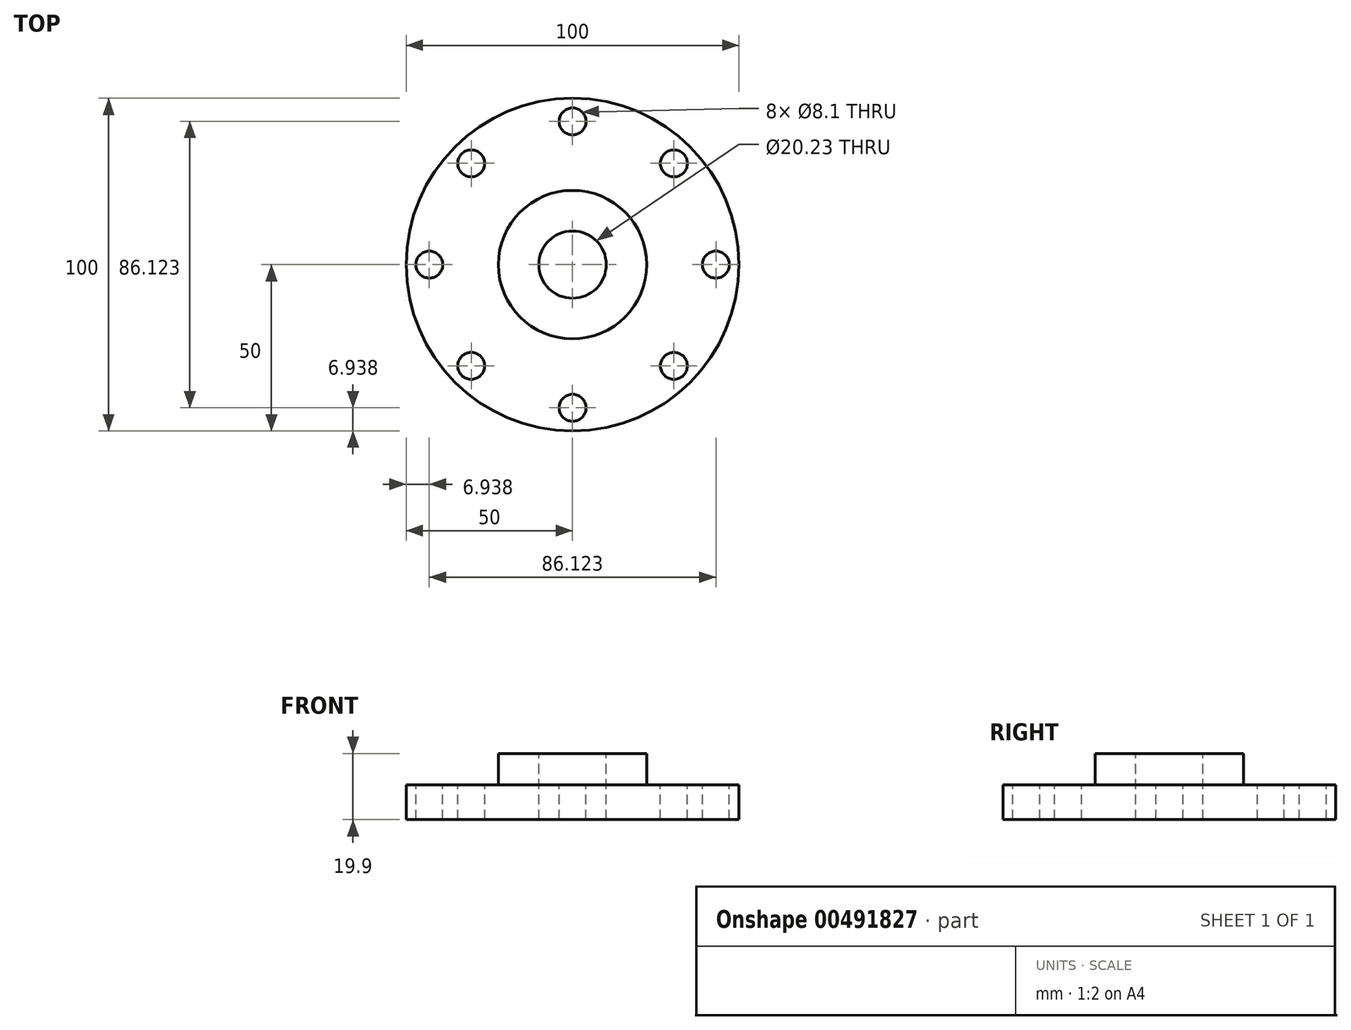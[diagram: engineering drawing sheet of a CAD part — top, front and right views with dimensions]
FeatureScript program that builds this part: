
annotation { "Feature Type Name" : "Feature", "Feature Type Description" : "" }
export const myFeature = defineFeature(function(context is Context, id is Id, definition is map)
    precondition{}
    {
        {
            var Q0;
            Q0=qCreatedBy(makeId("Top.planeOp"),FACE);
            var sketch = newSketch(context, id + "F0", { "sketchPlane" : qUnion([Q0])});
            skCircle(sketch, "E0", {"center": v(0, 0) * mm, "radius": 50 * mm});
            skSolve(sketch);
        }
        {
            var Q0;
            Q0=makeQuery(id+"F0.imprint","IMPRINT",FACE,{"disambiguationData":[TD([[makeQuery(id+"F0.imprint","IMPRINT",EDGE,{"derivedFrom":sQuery(id+"F0.wireOp",EDGE,"E0")}),1.0]])]});
            extrude(context, id + "F1", {"entities" : qUnion([Q0]), "depth" : 10.5 * mm});
        }
        {
            var Q0;
            Q0=makeQuery(id+"F1.opExtrude","CAP_FACE",FACE,{"disambiguationData":[OSD([sQuery(id+"F0.wireOp",EDGE,"E0")])],"isStart":false});
            var sketch = newSketch(context, id + "F2", { "sketchPlane" : qUnion([Q0])});
            skCircle(sketch, "E1", {"center": v(0, 0) * mm, "radius": 22.3 * mm});
            skSolve(sketch);
        }
        {
            var Q0;
            Q0=makeQuery(id+"F2.imprint","IMPRINT",FACE,{"disambiguationData":[TD([[makeQuery(id+"F2.imprint","IMPRINT",EDGE,{"derivedFrom":sQuery(id+"F2.wireOp",EDGE,"E1")}),1.0]])]});
            extrude(context, id + "F3", {"entities" : qUnion([Q0]), "operationType" : NewBodyOperationType.ADD, "depth" : 9.4 * mm});
        }
        {
            var Q0;
            Q0=makeQuery(id+"F1.opExtrude","CAP_FACE",FACE,{"disambiguationData":[OSD([sQuery(id+"F0.wireOp",EDGE,"E0")])],"isStart":false});
            var sketch = newSketch(context, id + "F4", { "sketchPlane" : qUnion([Q0])});
            skCircle(sketch, "E2", {"center": v(0, 0) * mm, "radius": 43 * mm});
            skSolve(sketch);
        }
        {
            var Q0;
            Q0=makeQuery(id+"F4.imprint","IMPRINT",FACE,{"disambiguationData":[TD([[makeQuery(id+"F4.imprint","IMPRINT",EDGE,{"derivedFrom":sQuery(id+"F4.wireOp",EDGE,"E2")}),1.0]])]});
            var sketch = newSketch(context, id + "F5", { "sketchPlane" : qUnion([Q0])});
            skLineSegment(sketch, "E3", {"start": v(0, 0) * mm, "end": v(0, 50.06) * mm});
            skLineSegment(sketch, "E4", {"start": v(0, 0) * mm, "end": v(49.33, 0) * mm});
            skLineSegment(sketch, "E5", {"start": v(0, 0) * mm, "end": v(-49.82, 0) * mm});
            skLineSegment(sketch, "E6", {"start": v(0, 0) * mm, "end": v(0, -49.83) * mm});
            skCircle(sketch, "E7", {"center": v(0, 43.06) * mm, "radius": 4.05 * mm});
            skCircle(sketch, "E8.1.0", {"center": v(-30.45, 30.45) * mm, "radius": 4.05 * mm});
            skCircle(sketch, "E8.2.0", {"center": v(-43.06, 0) * mm, "radius": 4.05 * mm});
            skCircle(sketch, "E8.3.0", {"center": v(-30.45, -30.45) * mm, "radius": 4.05 * mm});
            skCircle(sketch, "E8.4.0", {"center": v(0, -43.06) * mm, "radius": 4.05 * mm});
            skCircle(sketch, "E8.5.0", {"center": v(30.45, -30.45) * mm, "radius": 4.05 * mm});
            skCircle(sketch, "E8.6.0", {"center": v(43.06, 0) * mm, "radius": 4.05 * mm});
            skCircle(sketch, "E8.7.0", {"center": v(30.45, 30.45) * mm, "radius": 4.05 * mm});
            skPoint(sketch, "E8.center", {"position": v(0, 0) * mm});
            skSolve(sketch);
        }
        {
            var Q0;
            Q0=sQuery(id+"F5.wireOp",VERTEX,"E7.center");
            var Q1;
            Q1=sQuery(id+"F5.wireOp",VERTEX,"E8.7.0.center");
            var Q2;
            Q2=sQuery(id+"F5.wireOp",VERTEX,"E8.6.0.center");
            var Q3;
            Q3=sQuery(id+"F5.wireOp",VERTEX,"E8.5.0.center");
            var Q4;
            Q4=sQuery(id+"F5.wireOp",VERTEX,"E8.4.0.center");
            var Q5;
            Q5=sQuery(id+"F5.wireOp",VERTEX,"E8.3.0.center");
            var Q6;
            Q6=sQuery(id+"F5.wireOp",VERTEX,"E8.2.0.center");
            var Q7;
            Q7=sQuery(id+"F5.wireOp",VERTEX,"E8.1.0.center");
            var Q8;
            Q8=makeQuery(id+"F1.opExtrude","SWEPT_BODY",BODY,{"disambiguationData":[OSD([sQuery(id+"F0.wireOp",EDGE,"E0")])]});
            hole(context, id + "F6", {"style" : HoleStyle.SIMPLE, "endStyle" : HoleEndStyle.THROUGH, "holeDiameter" : 8.1 * mm, "locations" : qUnion([Q0, Q1, Q2, Q3, Q4, Q5, Q6, Q7]), "scope" : qUnion([Q8]), "isTappedThrough" : true});
        }
        {
            var Q0;
            Q0=makeQuery(id+"F3.opExtrude","CAP_FACE",FACE,{"disambiguationData":[OSD([sQuery(id+"F2.wireOp",EDGE,"E1")])],"isStart":false});
            var sketch = newSketch(context, id + "F7", { "sketchPlane" : qUnion([Q0])});
            skCircle(sketch, "E9", {"center": v(0, 0) * mm, "radius": 10.12 * mm});
            skSolve(sketch);
        }
        {
            var Q0;
            Q0=makeQuery(id+"F7.imprint","IMPRINT",FACE,{"disambiguationData":[TD([[makeQuery(id+"F7.imprint","IMPRINT",EDGE,{"derivedFrom":sQuery(id+"F7.wireOp",EDGE,"E9")}),1.0]])]});
            extrude(context, id + "F8", {"entities" : qUnion([Q0]), "operationType" : NewBodyOperationType.REMOVE, "oppositeDirection" : true, "depth" : 25 * mm});
        }
    });
